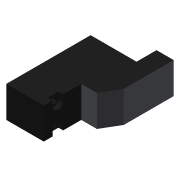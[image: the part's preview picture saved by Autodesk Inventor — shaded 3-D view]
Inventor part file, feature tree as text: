
AUTODESK INVENTOR PART (.ipt)
format: ipt  version: 2016 (Build 200138000, 138)  size: 140,800 bytes
history: native  units: mm
features: extrude x2, hole x2, mirror x1, sketch x1
ambient origin geometry x8: Origin, YZ Plane, XZ Plane, XY Plane, X Axis, Y Axis, Z Axis, Center Point
bodies: Volumenkörper1 (feature_tree)
feature tree (6):
  extrude  "Extrusion1"  Depth=14.7mm
  hole  "Bohrung1"  [1 undecoded]
  extrude  "Extrusion2"  Depth=27.0mm
  mirror  "Spiegeln1"
  hole  "Bohrung2"  [1 undecoded]
  sketch  "Skizze2"  dims[d0=5.5mm d1=14.7mm d3=12.0mm d4=27.0mm d5=12.0mm d6=5.0mm d7=6.4mm d8=16.0mm d9=10.0mm d10=0.0mm d11=1.75mm d12=4.5mm d13=2.0mm d14=6.0mm d15=3.4mm d16=1.5mm d17=90.0deg d18=8.0mm d19=20.594885mm d20=10.0mm d21=0.0mm d22=2.5mm d23=2.5mm d24=2.8mm d25=7.8mm d26=5.0mm d27=5.3mm d28=1.5mm d29=6.0mm d30=4.0mm d31=2.0mm d32=90.0deg d33=8.0mm d34=20.594885mm d35=0.8mm]
note: 2 required parameter values undecoded (feature->parameter linkage not recoverable at this tier; creation-order binding heuristic only, values carry confidence <= 0.55)
